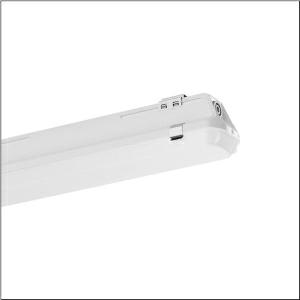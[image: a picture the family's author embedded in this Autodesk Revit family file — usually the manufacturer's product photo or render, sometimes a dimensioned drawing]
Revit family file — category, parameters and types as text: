
# Revit family: monsun_r__11_51fp10dp660h_8765
name_source: partatom
category: Lighting Fixtures
units: mm (PartAtom-declared; Revit-internal decimal feet)

## family parameters
Cut with Voids When Loaded = No
Host = Face
Light Source = No
Part Type = Normal
Room Calculation Point = No
Round Connector Dimension = Use Diameter
Shared = No

## types (1)
- --- (1 x LED, 5970 lm, 34.6 W, 6500K)
    Apparent Load = 35 VA
    CIE Flux Codes = 47 77 93 94 100
    Color Rendering = 80
    Color Temperature = 6500K
    Default Elevation = 1800 mm
    Description = Monsun® 11, damp-proof luminaire, chain hanger, primary optical cover: enclosure, of PMMA, light emission: direct distribution, primary light characteristic: symmetric, installation type: suspended mounting, surface-mounted, horizontal mounting, vertical mounting, LED, rated luminous flux: 5.970lm, luminous efficacy: 173lm/W, light colour: 865, colour temperature: 6500K, control gear: ECG DALI, with terminal, 5-pole, max. 2.5mm², mains connection: 220..240V, AC, 50/60Hz, rated input power: 35W, luminaire housing, of glass-fibre reinforced polyester, uncoated, bright grey, incl. chain hanger, length: 1.590mm, width: 90mm, height: 88mm, clip for enclosure, of stainless steel (V2A), ceiling mounting element, of stainless steel (V2A), chain hanger, of stainless steel (V2A), protection rating (complete): IP66, insulation class (complete): insulation class I (protective earthing), certification: CE, ENEC, VDE, UKCA, protection symbol: D, impact resistance: IK04, permissible operating ambient temperature: -25..+40°C, standard: EN 50419, EN 60598-2-1, no direct snow, no direct sun, no direct rain, for indoor or canopied outdoor use, corresponds to IFS (International Featured Standards) requirements for safety and quality in the food industry, contact your sales advisor before using the luminaires in applications with unclear chemical exposure, large temperature fluctuations or condensation-forming humidity, LABS conformity tested according to VDMA 24364:2018-05, packaging unit: 1 piece
    Height = 89 mm
    Lamp = 1 x LED
    Lamp Light Flux = 5970 lm
    Lamp Power = 34.6 W
    Lamp count = 1
    Length = 1590 mm
    Luminous efficacy = 173 lm/W
    Manufacturer = Siteco
    ModVariant = No
    Model = 51FP10DP660H
    Mounting Place = Ceiling
    Mounting Type = Surface mounted
    Number of Poles = 1
    OnlyDefault = Yes
    Power Factor = 1
    Product Name = Monsun® 11
    Product group = damp-proof luminaire
    ProductGroupID = 300
    Protection Class = Protection class I
    Protection Degree = IP 66
    RLX_Detail_Level = 1
    RLX_Emergency_Light_Flux = 0 lm
    RLX_Emergency_Type = 0
    RLX_Emergency_Type_DB = No
    RlxData = <blob elided: 92325 chars, md5=2b0ea27b>
    Socket = socket
    Standby Power = 0 W
    System Light Flux = 5970 lm
    System Power = 35 W
    Type Comments = factory setting: luminous flux: 100 % | dim-lin: 254 | 232 mA
    Type Image = l_1004748.jpg
    URL = http://relux.com
    VarID = @adj_142183
    Voltage = 0 V
    Weight = 0.00 kg
    Width = 90 mm

## geometry (parser evidence)
native form markers: Blend x4, Sweep x13
no freeform markers — native parametric forms only
